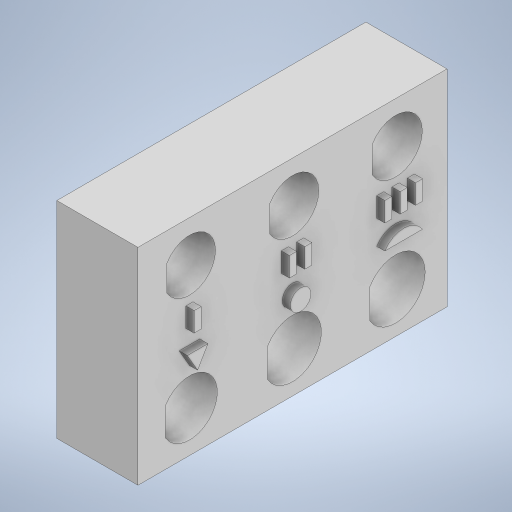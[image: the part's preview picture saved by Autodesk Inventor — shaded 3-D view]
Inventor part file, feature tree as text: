
AUTODESK INVENTOR PART (.ipt)
format: ipt  version: 2023 (Build 270158000, 158)  size: 348,672 bytes
history: native  units: in
note: dims shown in document units (in); Inventor stores cm internally (conversion verified against a paired STEP export)
features: extrude x2, sketch x1
ambient origin geometry x8: Origin, YZ Plane, XZ Plane, XY Plane, X Axis, Y Axis, Z Axis, Center Point
bodies: Solid1 (feature_tree)
feature tree (3):
  sketch  "Sketch1"  dims[d0=0.2525in d1=0.1263in d2=0.255in d3=0.1275in d4=0.26in d5=0.13in d6=0.27in d7=0.135in d8=0.28in d9=0.14in d10=0.2875in d11=0.1438in d12=1.5in d13=0.25in d14=0.25in d15=0.2in d16=1.0in d17=0.2in d18=0.0344in d19=0.0947in d20=0.09in d21=0.0344in d22=0.0947in d23=0.0344in d24=0.0947in d25=0.02in d26=0.02in d27=0.0344in d28=0.0947in d29=0.0344in d30=0.0947in d31=0.0344in d32=0.0947in d33=0.04in d35=0.04in d36=0.1in d38=0.1in d39=0.1in d40=0.035in d41=0.1in d42=0.075in d43=0.1833in d44=0.109in d45=0.224in d46=0.25in d47=0.3937in d48=0.0in d49=0.4331in d50=0.0in]
  extrude  "Extrusion1"  Depth=0.1275in
  extrude  "Extrusion2"  Depth=0.13in
